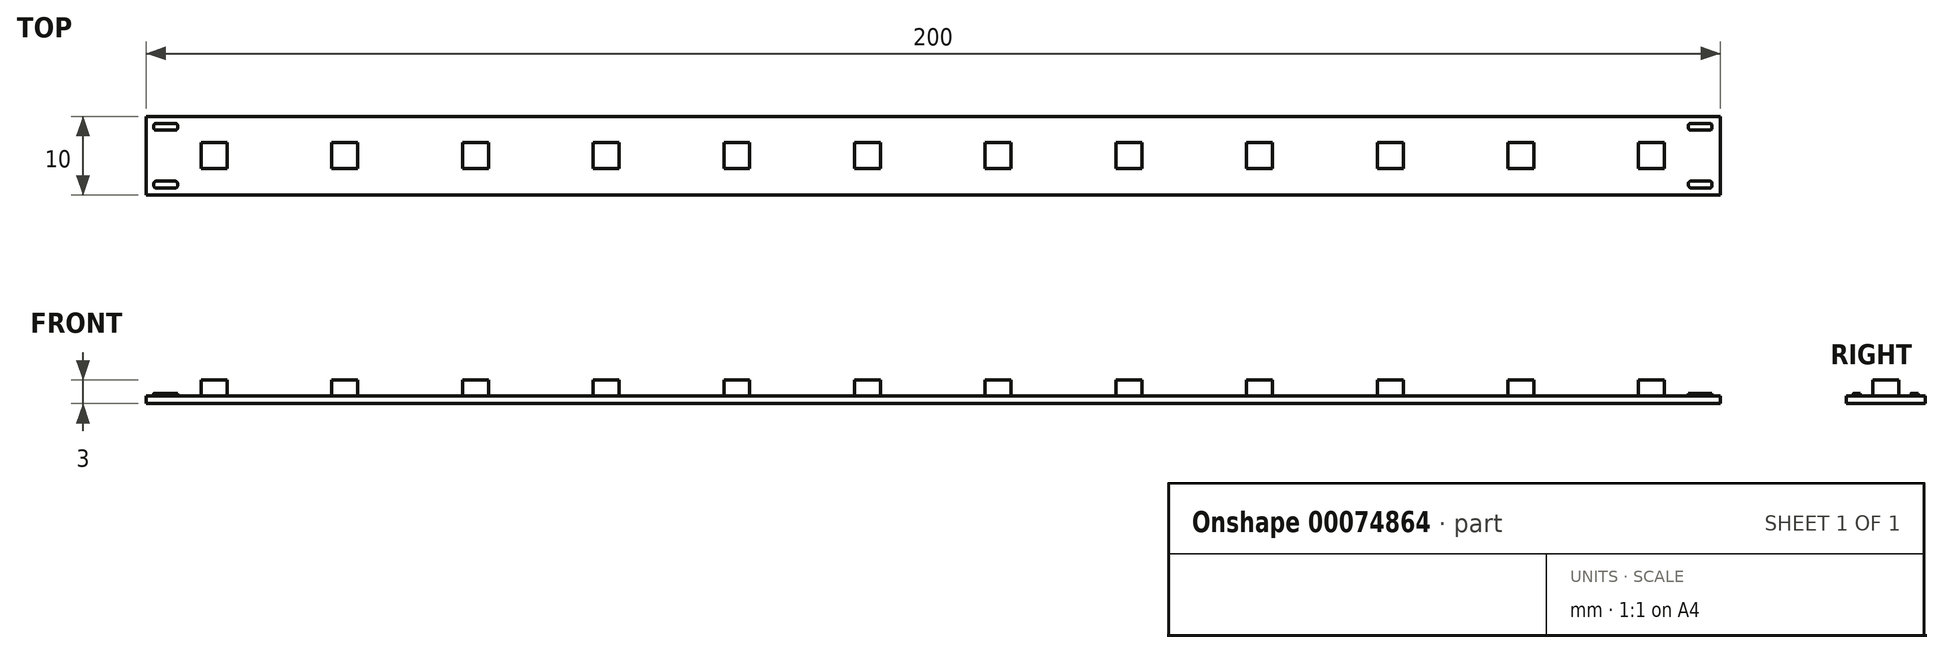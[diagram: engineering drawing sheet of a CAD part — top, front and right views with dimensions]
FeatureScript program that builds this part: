
annotation { "Feature Type Name" : "Feature", "Feature Type Description" : "" }
export const myFeature = defineFeature(function(context is Context, id is Id, definition is map)
    precondition{}
    {
        {
            var Q0;
            Q0=qCreatedBy(makeId("Top.planeOp"),FACE);
            var sketch = newSketch(context, id + "F0", { "sketchPlane" : qUnion([Q0])});
            skLineSegment(sketch, "E0.bottom", {"start": v(0, 0) * mm, "end": v(200, 0) * mm});
            skLineSegment(sketch, "E0.top", {"start": v(0, 10) * mm, "end": v(200, 10) * mm});
            skLineSegment(sketch, "E0.left", {"start": v(0, 0) * mm, "end": v(0, 10) * mm});
            skLineSegment(sketch, "E0.right", {"start": v(200, 0) * mm, "end": v(200, 10) * mm});
            skSolve(sketch);
        }
        {
            var Q0;
            Q0=makeQuery(id+"F0.imprint","IMPRINT",FACE,{"disambiguationData":[TD([[makeQuery(id+"F0.imprint","IMPRINT",EDGE,{"derivedFrom":sQuery(id+"F0.wireOp",EDGE,"E0.bottom")}),1.0]])]});
            extrude(context, id + "F1", {"entities" : qUnion([Q0]), "depth" : 1 * mm});
        }
        {
            var Q0;
            Q0=makeQuery(id+"F1.opExtrude","CAP_FACE",FACE,{"disambiguationData":[OSD([sQuery(id+"F0.wireOp",EDGE,"E0.bottom"),sQuery(id+"F0.wireOp",EDGE,"E0.top"),sQuery(id+"F0.wireOp",EDGE,"E0.left"),sQuery(id+"F0.wireOp",EDGE,"E0.right")])],"isStart":false});
            var sketch = newSketch(context, id + "F2", { "sketchPlane" : qUnion([Q0])});
            skLineSegment(sketch, "E1.bottom", {"start": v(7, 6.65) * mm, "end": v(10.3, 6.65) * mm});
            skLineSegment(sketch, "E1.top", {"start": v(7, 3.35) * mm, "end": v(10.3, 3.35) * mm});
            skLineSegment(sketch, "E1.left", {"start": v(7, 6.65) * mm, "end": v(7, 3.35) * mm});
            skLineSegment(sketch, "E1.right", {"start": v(10.3, 6.65) * mm, "end": v(10.3, 3.35) * mm});
            skLineSegment(sketch, "E2.1.0.0", {"start": v(23.6, 6.65) * mm, "end": v(26.9, 6.65) * mm});
            skLineSegment(sketch, "E2.1.0.1", {"start": v(23.6, 6.65) * mm, "end": v(23.6, 3.35) * mm});
            skLineSegment(sketch, "E2.1.0.2", {"start": v(23.6, 3.35) * mm, "end": v(26.9, 3.35) * mm});
            skLineSegment(sketch, "E2.1.0.3", {"start": v(26.9, 6.65) * mm, "end": v(26.9, 3.35) * mm});
            skLineSegment(sketch, "E2.2.0.0", {"start": v(40.2, 6.65) * mm, "end": v(43.5, 6.65) * mm});
            skLineSegment(sketch, "E2.2.0.1", {"start": v(40.2, 6.65) * mm, "end": v(40.2, 3.35) * mm});
            skLineSegment(sketch, "E2.2.0.2", {"start": v(40.2, 3.35) * mm, "end": v(43.5, 3.35) * mm});
            skLineSegment(sketch, "E2.2.0.3", {"start": v(43.5, 6.65) * mm, "end": v(43.5, 3.35) * mm});
            skLineSegment(sketch, "E2.3.0.0", {"start": v(56.8, 6.65) * mm, "end": v(60.1, 6.65) * mm});
            skLineSegment(sketch, "E2.3.0.1", {"start": v(56.8, 6.65) * mm, "end": v(56.8, 3.35) * mm});
            skLineSegment(sketch, "E2.3.0.2", {"start": v(56.8, 3.35) * mm, "end": v(60.1, 3.35) * mm});
            skLineSegment(sketch, "E2.3.0.3", {"start": v(60.1, 6.65) * mm, "end": v(60.1, 3.35) * mm});
            skLineSegment(sketch, "E2.4.0.0", {"start": v(73.4, 6.65) * mm, "end": v(76.7, 6.65) * mm});
            skLineSegment(sketch, "E2.4.0.1", {"start": v(73.4, 6.65) * mm, "end": v(73.4, 3.35) * mm});
            skLineSegment(sketch, "E2.4.0.2", {"start": v(73.4, 3.35) * mm, "end": v(76.7, 3.35) * mm});
            skLineSegment(sketch, "E2.4.0.3", {"start": v(76.7, 6.65) * mm, "end": v(76.7, 3.35) * mm});
            skLineSegment(sketch, "E2.5.0.0", {"start": v(90, 6.65) * mm, "end": v(93.3, 6.65) * mm});
            skLineSegment(sketch, "E2.5.0.1", {"start": v(90, 6.65) * mm, "end": v(90, 3.35) * mm});
            skLineSegment(sketch, "E2.5.0.2", {"start": v(90, 3.35) * mm, "end": v(93.3, 3.35) * mm});
            skLineSegment(sketch, "E2.5.0.3", {"start": v(93.3, 6.65) * mm, "end": v(93.3, 3.35) * mm});
            skLineSegment(sketch, "E2.6.0.0", {"start": v(106.6, 6.65) * mm, "end": v(109.9, 6.65) * mm});
            skLineSegment(sketch, "E2.6.0.1", {"start": v(106.6, 6.65) * mm, "end": v(106.6, 3.35) * mm});
            skLineSegment(sketch, "E2.6.0.2", {"start": v(106.6, 3.35) * mm, "end": v(109.9, 3.35) * mm});
            skLineSegment(sketch, "E2.6.0.3", {"start": v(109.9, 6.65) * mm, "end": v(109.9, 3.35) * mm});
            skLineSegment(sketch, "E2.7.0.0", {"start": v(123.2, 6.65) * mm, "end": v(126.5, 6.65) * mm});
            skLineSegment(sketch, "E2.7.0.1", {"start": v(123.2, 6.65) * mm, "end": v(123.2, 3.35) * mm});
            skLineSegment(sketch, "E2.7.0.2", {"start": v(123.2, 3.35) * mm, "end": v(126.5, 3.35) * mm});
            skLineSegment(sketch, "E2.7.0.3", {"start": v(126.5, 6.65) * mm, "end": v(126.5, 3.35) * mm});
            skLineSegment(sketch, "E2.8.0.0", {"start": v(139.8, 6.65) * mm, "end": v(143.1, 6.65) * mm});
            skLineSegment(sketch, "E2.8.0.1", {"start": v(139.8, 6.65) * mm, "end": v(139.8, 3.35) * mm});
            skLineSegment(sketch, "E2.8.0.2", {"start": v(139.8, 3.35) * mm, "end": v(143.1, 3.35) * mm});
            skLineSegment(sketch, "E2.8.0.3", {"start": v(143.1, 6.65) * mm, "end": v(143.1, 3.35) * mm});
            skLineSegment(sketch, "E2.9.0.0", {"start": v(156.4, 6.65) * mm, "end": v(159.7, 6.65) * mm});
            skLineSegment(sketch, "E2.9.0.1", {"start": v(156.4, 6.65) * mm, "end": v(156.4, 3.35) * mm});
            skLineSegment(sketch, "E2.9.0.2", {"start": v(156.4, 3.35) * mm, "end": v(159.7, 3.35) * mm});
            skLineSegment(sketch, "E2.9.0.3", {"start": v(159.7, 6.65) * mm, "end": v(159.7, 3.35) * mm});
            skLineSegment(sketch, "E2.10.0.0", {"start": v(173, 6.65) * mm, "end": v(176.3, 6.65) * mm});
            skLineSegment(sketch, "E2.10.0.1", {"start": v(173, 6.65) * mm, "end": v(173, 3.35) * mm});
            skLineSegment(sketch, "E2.10.0.2", {"start": v(173, 3.35) * mm, "end": v(176.3, 3.35) * mm});
            skLineSegment(sketch, "E2.10.0.3", {"start": v(176.3, 6.65) * mm, "end": v(176.3, 3.35) * mm});
            skLineSegment(sketch, "E2.11.0.0", {"start": v(189.6, 6.65) * mm, "end": v(192.9, 6.65) * mm});
            skLineSegment(sketch, "E2.11.0.1", {"start": v(189.6, 6.65) * mm, "end": v(189.6, 3.35) * mm});
            skLineSegment(sketch, "E2.11.0.2", {"start": v(189.6, 3.35) * mm, "end": v(192.9, 3.35) * mm});
            skLineSegment(sketch, "E2.11.0.3", {"start": v(192.9, 6.65) * mm, "end": v(192.9, 3.35) * mm});
            skLineSegment(sketch, "E2.direction1", {"start": v(7, 6.65) * mm, "end": v(23.6, 6.65) * mm, "construction": true});
            skSolve(sketch);
        }
        {
            var Q0;
            Q0=makeQuery(id+"F2.imprint","IMPRINT",FACE,{"disambiguationData":[TD([[makeQuery(id+"F2.imprint","IMPRINT",EDGE,{"derivedFrom":sQuery(id+"F2.wireOp",EDGE,"E1.bottom")}),-1.0]])]});
            var Q1;
            Q1=makeQuery(id+"F2.imprint","IMPRINT",FACE,{"disambiguationData":[TD([[makeQuery(id+"F2.imprint","IMPRINT",EDGE,{"derivedFrom":sQuery(id+"F2.wireOp",EDGE,"E2.1.0.0")}),-1.0]])]});
            var Q2;
            Q2=makeQuery(id+"F2.imprint","IMPRINT",FACE,{"disambiguationData":[TD([[makeQuery(id+"F2.imprint","IMPRINT",EDGE,{"derivedFrom":sQuery(id+"F2.wireOp",EDGE,"E2.2.0.0")}),-1.0]])]});
            var Q3;
            Q3=makeQuery(id+"F2.imprint","IMPRINT",FACE,{"disambiguationData":[TD([[makeQuery(id+"F2.imprint","IMPRINT",EDGE,{"derivedFrom":sQuery(id+"F2.wireOp",EDGE,"E2.3.0.0")}),-1.0]])]});
            var Q4;
            Q4=makeQuery(id+"F2.imprint","IMPRINT",FACE,{"disambiguationData":[TD([[makeQuery(id+"F2.imprint","IMPRINT",EDGE,{"derivedFrom":sQuery(id+"F2.wireOp",EDGE,"E2.4.0.0")}),-1.0]])]});
            var Q5;
            Q5=makeQuery(id+"F2.imprint","IMPRINT",FACE,{"disambiguationData":[TD([[makeQuery(id+"F2.imprint","IMPRINT",EDGE,{"derivedFrom":sQuery(id+"F2.wireOp",EDGE,"E2.5.0.0")}),-1.0]])]});
            var Q6;
            Q6=makeQuery(id+"F2.imprint","IMPRINT",FACE,{"disambiguationData":[TD([[makeQuery(id+"F2.imprint","IMPRINT",EDGE,{"derivedFrom":sQuery(id+"F2.wireOp",EDGE,"E2.6.0.0")}),-1.0]])]});
            var Q7;
            Q7=makeQuery(id+"F2.imprint","IMPRINT",FACE,{"disambiguationData":[TD([[makeQuery(id+"F2.imprint","IMPRINT",EDGE,{"derivedFrom":sQuery(id+"F2.wireOp",EDGE,"E2.7.0.0")}),-1.0]])]});
            var Q8;
            Q8=makeQuery(id+"F2.imprint","IMPRINT",FACE,{"disambiguationData":[TD([[makeQuery(id+"F2.imprint","IMPRINT",EDGE,{"derivedFrom":sQuery(id+"F2.wireOp",EDGE,"E2.8.0.0")}),-1.0]])]});
            var Q9;
            Q9=makeQuery(id+"F2.imprint","IMPRINT",FACE,{"disambiguationData":[TD([[makeQuery(id+"F2.imprint","IMPRINT",EDGE,{"derivedFrom":sQuery(id+"F2.wireOp",EDGE,"E2.9.0.0")}),-1.0]])]});
            var Q10;
            Q10=makeQuery(id+"F2.imprint","IMPRINT",FACE,{"disambiguationData":[TD([[makeQuery(id+"F2.imprint","IMPRINT",EDGE,{"derivedFrom":sQuery(id+"F2.wireOp",EDGE,"E2.10.0.0")}),-1.0]])]});
            var Q11;
            Q11=makeQuery(id+"F2.imprint","IMPRINT",FACE,{"disambiguationData":[TD([[makeQuery(id+"F2.imprint","IMPRINT",EDGE,{"derivedFrom":sQuery(id+"F2.wireOp",EDGE,"E2.11.0.0")}),-1.0]])]});
            extrude(context, id + "F3", {"entities" : qUnion([Q0, Q1, Q2, Q3, Q4, Q5, Q6, Q7, Q8, Q9, Q10, Q11]), "operationType" : NewBodyOperationType.ADD, "depth" : 2 * mm});
        }
        {
            var Q0;
            Q0=makeQuery(id+"F1.opExtrude","CAP_FACE",FACE,{"disambiguationData":[OSD([sQuery(id+"F0.wireOp",EDGE,"E0.bottom"),sQuery(id+"F0.wireOp",EDGE,"E0.top"),sQuery(id+"F0.wireOp",EDGE,"E0.left"),sQuery(id+"F0.wireOp",EDGE,"E0.right")])],"isStart":false});
            var sketch = newSketch(context, id + "F4", { "sketchPlane" : qUnion([Q0])});
            skLineSegment(sketch, "E3.bottom", {"start": v(1.3, 0.88) * mm, "end": v(3.7, 0.88) * mm});
            skLineSegment(sketch, "E3.top", {"start": v(1.3, 1.76) * mm, "end": v(3.7, 1.76) * mm});
            skLineSegment(sketch, "E3.left", {"start": v(1, 1.18) * mm, "end": v(1, 1.46) * mm});
            skLineSegment(sketch, "E3.right", {"start": v(4, 1.18) * mm, "end": v(4, 1.46) * mm});
            skLineSegment(sketch, "E4.0.1.0", {"start": v(4, 8.53) * mm, "end": v(4, 8.81) * mm});
            skLineSegment(sketch, "E4.0.1.1", {"start": v(1, 8.53) * mm, "end": v(1, 8.81) * mm});
            skLineSegment(sketch, "E4.0.1.2", {"start": v(1.3, 9.11) * mm, "end": v(3.7, 9.11) * mm});
            skLineSegment(sketch, "E4.0.1.3", {"start": v(1.3, 8.23) * mm, "end": v(3.7, 8.23) * mm});
            skLineSegment(sketch, "E4.1.0.0", {"start": v(198.93, 1.18) * mm, "end": v(198.93, 1.46) * mm});
            skLineSegment(sketch, "E4.1.0.1", {"start": v(195.93, 1.28) * mm, "end": v(195.93, 1.46) * mm});
            skLineSegment(sketch, "E4.1.0.2", {"start": v(196.23, 1.76) * mm, "end": v(198.63, 1.76) * mm});
            skLineSegment(sketch, "E4.1.0.3", {"start": v(196.33, 0.88) * mm, "end": v(198.63, 0.88) * mm});
            skLineSegment(sketch, "E4.1.1.0", {"start": v(198.93, 8.53) * mm, "end": v(198.93, 8.81) * mm});
            skLineSegment(sketch, "E4.1.1.1", {"start": v(195.93, 8.53) * mm, "end": v(195.93, 8.81) * mm});
            skLineSegment(sketch, "E4.1.1.2", {"start": v(196.23, 9.11) * mm, "end": v(198.63, 9.11) * mm});
            skLineSegment(sketch, "E4.1.1.3", {"start": v(196.23, 8.23) * mm, "end": v(198.63, 8.23) * mm});
            skLineSegment(sketch, "E4.direction1", {"start": v(4, 0.88) * mm, "end": v(198.93, 0.88) * mm, "construction": true});
            skLineSegment(sketch, "E4.direction2", {"start": v(4, 0.88) * mm, "end": v(4, 8.23) * mm, "construction": true});
            skPoint(sketch, "E5.visualSharp", {"position": v(1, 1.76) * mm});
            skArc(sketch, "E5.filletArc", {"start": v(1.3, 1.76) * mm, "mid": v(1.09, 1.67) * mm, "end": v(1, 1.46) * mm});
            skPoint(sketch, "E6.visualSharp", {"position": v(4, 1.76) * mm});
            skArc(sketch, "E6.filletArc", {"start": v(4, 1.46) * mm, "mid": v(3.91, 1.67) * mm, "end": v(3.7, 1.76) * mm});
            skPoint(sketch, "E7.visualSharp", {"position": v(4, 0.88) * mm});
            skArc(sketch, "E7.filletArc", {"start": v(3.7, 0.88) * mm, "mid": v(3.91, 0.97) * mm, "end": v(4, 1.18) * mm});
            skPoint(sketch, "E8.visualSharp", {"position": v(1, 0.88) * mm});
            skArc(sketch, "E8.filletArc", {"start": v(1, 1.18) * mm, "mid": v(1.09, 0.97) * mm, "end": v(1.3, 0.88) * mm});
            skPoint(sketch, "E9.visualSharp", {"position": v(1, 8.23) * mm});
            skArc(sketch, "E9.filletArc", {"start": v(1, 8.53) * mm, "mid": v(1.09, 8.32) * mm, "end": v(1.3, 8.23) * mm});
            skPoint(sketch, "E10.visualSharp", {"position": v(4, 9.11) * mm});
            skArc(sketch, "E10.filletArc", {"start": v(4, 8.81) * mm, "mid": v(3.91, 9.02) * mm, "end": v(3.7, 9.11) * mm});
            skPoint(sketch, "E11.visualSharp", {"position": v(4, 8.23) * mm});
            skArc(sketch, "E11.filletArc", {"start": v(3.7, 8.23) * mm, "mid": v(3.91, 8.32) * mm, "end": v(4, 8.53) * mm});
            skPoint(sketch, "E12.visualSharp", {"position": v(1, 9.11) * mm});
            skArc(sketch, "E12.filletArc", {"start": v(1.3, 9.11) * mm, "mid": v(1.09, 9.02) * mm, "end": v(1, 8.81) * mm});
            skPoint(sketch, "E13.visualSharp", {"position": v(198.93, 1.76) * mm});
            skArc(sketch, "E13.filletArc", {"start": v(198.93, 1.46) * mm, "mid": v(198.84, 1.67) * mm, "end": v(198.63, 1.76) * mm});
            skPoint(sketch, "E14.visualSharp", {"position": v(195.93, 0.88) * mm});
            skArc(sketch, "E14.filletArc", {"start": v(195.93, 1.28) * mm, "mid": v(196.05, 1) * mm, "end": v(196.33, 0.88) * mm});
            skPoint(sketch, "E15.visualSharp", {"position": v(195.93, 1.76) * mm});
            skArc(sketch, "E15.filletArc", {"start": v(196.23, 1.76) * mm, "mid": v(196.02, 1.67) * mm, "end": v(195.93, 1.46) * mm});
            skPoint(sketch, "E16.visualSharp", {"position": v(198.93, 0.88) * mm});
            skArc(sketch, "E16.filletArc", {"start": v(198.63, 0.88) * mm, "mid": v(198.84, 0.97) * mm, "end": v(198.93, 1.18) * mm});
            skPoint(sketch, "E17.visualSharp", {"position": v(198.93, 8.23) * mm});
            skArc(sketch, "E17.filletArc", {"start": v(198.63, 8.23) * mm, "mid": v(198.84, 8.32) * mm, "end": v(198.93, 8.53) * mm});
            skPoint(sketch, "E18.visualSharp", {"position": v(195.93, 9.11) * mm});
            skArc(sketch, "E18.filletArc", {"start": v(196.23, 9.11) * mm, "mid": v(196.02, 9.02) * mm, "end": v(195.93, 8.81) * mm});
            skPoint(sketch, "E19.visualSharp", {"position": v(195.93, 8.23) * mm});
            skArc(sketch, "E19.filletArc", {"start": v(195.93, 8.53) * mm, "mid": v(196.02, 8.32) * mm, "end": v(196.23, 8.23) * mm});
            skPoint(sketch, "E20.visualSharp", {"position": v(198.93, 9.11) * mm});
            skArc(sketch, "E20.filletArc", {"start": v(198.93, 8.81) * mm, "mid": v(198.84, 9.02) * mm, "end": v(198.63, 9.11) * mm});
            skSolve(sketch);
        }
        {
            var Q0;
            Q0=makeQuery(id+"F4.imprint","IMPRINT",FACE,{"disambiguationData":[TD([[makeQuery(id+"F4.imprint","IMPRINT",EDGE,{"derivedFrom":sQuery(id+"F4.wireOp",EDGE,"E3.bottom")}),1.0]])]});
            var Q1;
            Q1=makeQuery(id+"F4.imprint","IMPRINT",FACE,{"disambiguationData":[TD([[makeQuery(id+"F4.imprint","IMPRINT",EDGE,{"derivedFrom":sQuery(id+"F4.wireOp",EDGE,"E4.1.1.0")}),1.0]])]});
            var Q2;
            Q2=makeQuery(id+"F4.imprint","IMPRINT",FACE,{"disambiguationData":[TD([[makeQuery(id+"F4.imprint","IMPRINT",EDGE,{"derivedFrom":sQuery(id+"F4.wireOp",EDGE,"E4.1.0.0")}),1.0]])]});
            var Q3;
            Q3=makeQuery(id+"F4.imprint","IMPRINT",FACE,{"disambiguationData":[TD([[makeQuery(id+"F4.imprint","IMPRINT",EDGE,{"derivedFrom":sQuery(id+"F4.wireOp",EDGE,"E4.0.1.0")}),1.0]])]});
            extrude(context, id + "F5", {"entities" : qUnion([Q0, Q1, Q2, Q3]), "operationType" : NewBodyOperationType.ADD, "depth" : 0.3 * mm});
        }
    });
